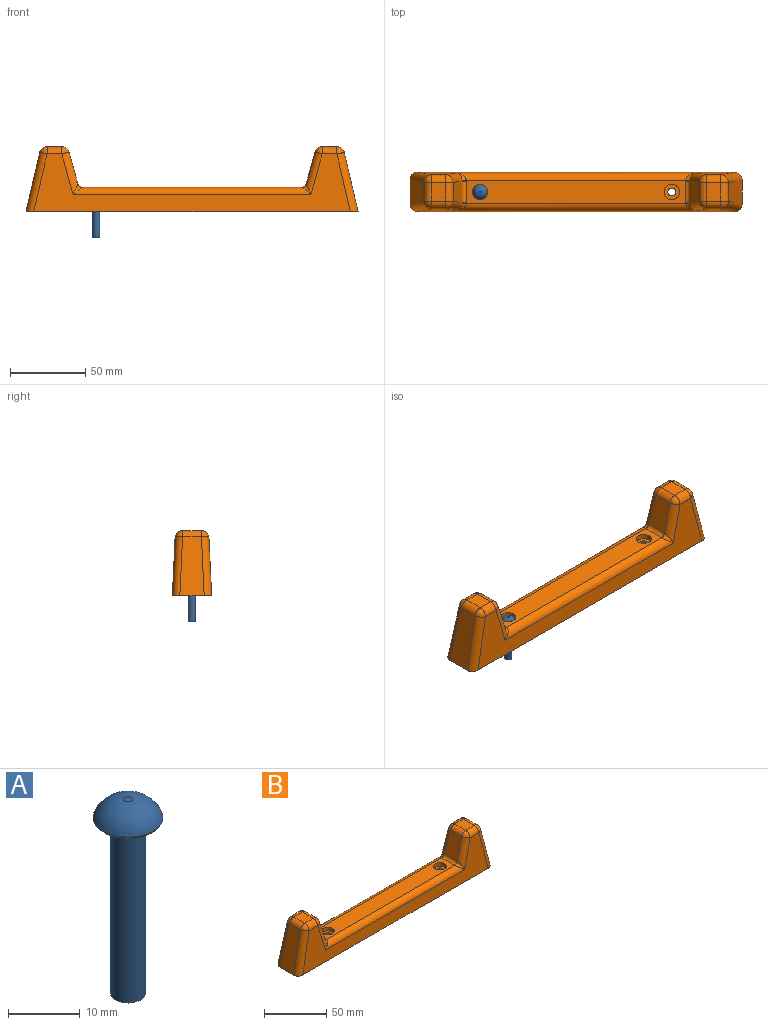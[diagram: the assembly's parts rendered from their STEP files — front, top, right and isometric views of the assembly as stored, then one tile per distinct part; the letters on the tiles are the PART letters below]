
ASSEMBLY  parts=2 mates=1
PART A: 6 faces, bbox 10.5x10.5x33 mm
  f0: cylinder r=2.45mm len=29.5mm, axis (0,0,-1), area 454.1mm2, adj f1,f2
  f1: plane 4.9x4.9mm, normal (0,0,-1), area 18.9mm2, adj f0
  f2: plane 8.7x8.7mm, normal (0,0,-1), area 40.6mm2, adj f0,f4
  f3: plane 1.21x1.21mm, normal (0,0,1), area 1.2mm2, adj f5
  f4: torus R=4.35mm, axis (0,0,1), area 23mm2, adj f2,f5
  f5: torus R=0.61mm, axis (0,0,-1), area 106mm2, adj f3,f4
PART B: 52 faces, bbox 220x26.1x43.9 mm
  f0: cylinder r=2.6mm len=12.5mm, axis (0,0,1), area 204.2mm2, adj f4,f14
  f1: cylinder r=2.6mm len=12.5mm, axis (0,0,1), area 204.2mm2, adj f4,f12
  f2: plane 12.45x9.73mm, normal (0,0,1), area 121.2mm2, adj f25,f26,f29,f30
  f3: plane 12.45x9.73mm, normal (0,0,1), area 121.2mm2, adj f33,f34,f37,f38
  f4: plane 220x26mm, normal (0,0,-1), area 5656mm2, adj f0,f1,f5,f6,f7,f8,f20,f21
  f5: plane 39.13x16.09mm, normal (-0.97,0,0.23), area 573.5mm2, adj f4,f22,f23,f30
  f6: plane 209.84x38.23mm, normal (0,-1,0.05), area 3228.5mm2, adj f4,f16,f17,f21,f22,f26,f33,f40
  f7: plane 39.13x16.09mm, normal (0.97,0,0.23), area 573.5mm2, adj f4,f20,f21,f37
  f8: plane 209.84x38.23mm, normal (0,1,0.05), area 3228.5mm2, adj f4,f18,f19,f20,f23,f29,f38,f41
  f9: plane 145.45x14.97mm, normal (0,0,1), area 2013.2mm2, adj f13,f15,f40,f41,f43,f44,f45,f48
  f10: plane 21.14x14.42mm, normal (-0.96,0,0.27), area 294.8mm2, adj f16,f18,f34,f44
  f11: plane 21.14x14.42mm, normal (0.96,0,0.27), area 294.8mm2, adj f17,f19,f25,f49
  f12: plane 10.2x10.2mm, normal (0,0,1), area 60.5mm2, adj f1,f13
  f13: cylinder r=5.1mm len=10.2mm, axis (0,0,1), area 112.2mm2, adj f9,f12
  f14: plane 10.2x10.2mm, normal (0,0,1), area 60.5mm2, adj f0,f15
  f15: cylinder r=5.1mm len=10.2mm, axis (0,0,1), area 112.2mm2, adj f9,f14
  f16: cylinder r=5mm len=28.12mm, axis (-0.27,-0.04,-0.96), area 188.5mm2, adj f6,f10,f32,f42,f43
  f17: cylinder r=5mm len=28.12mm, axis (0.27,-0.04,-0.96), area 188.5mm2, adj f6,f11,f24,f47,f48
  f18: cylinder r=5mm len=28.12mm, axis (-0.27,0.04,-0.96), area 188.5mm2, adj f8,f10,f36,f45,f46
  f19: cylinder r=5mm len=28.12mm, axis (0.27,0.04,-0.96), area 188.5mm2, adj f8,f11,f27,f50,f51
  f20: cylinder r=5mm len=40.08mm, axis (-0.23,-0.05,0.97), area 311.6mm2, adj f4,f7,f8,f39
  f21: cylinder r=5mm len=40.08mm, axis (0.23,-0.05,-0.97), area 311.6mm2, adj f4,f6,f7,f35
  f22: cylinder r=5mm len=40.08mm, axis (0.23,0.05,0.97), area 311.6mm2, adj f4,f5,f6,f28
  f23: cylinder r=5mm len=40.08mm, axis (-0.23,0.05,-0.97), area 311.6mm2, adj f4,f5,f8,f31
  f24: sphere r=5mm, area 31.4mm2, adj f17,f25,f26
  f25: cylinder r=5mm len=12.45mm, axis (0,1,0), area 80.9mm2, adj f2,f11,f24,f27
  f26: cylinder r=5mm len=9.73mm, axis (1,0,0), area 74.1mm2, adj f2,f6,f24,f28
  f27: sphere r=5mm, area 31.4mm2, adj f19,f25,f29
  f28: sphere r=5mm, area 32.4mm2, adj f22,f26,f30
  f29: cylinder r=5mm len=9.73mm, axis (1,0,0), area 74.1mm2, adj f2,f8,f27,f31
  f30: cylinder r=5mm len=12.45mm, axis (0,-1,0), area 83.6mm2, adj f2,f5,f28,f31
  f31: sphere r=5mm, area 32.4mm2, adj f23,f29,f30
  f32: sphere r=5mm, area 31.4mm2, adj f16,f33,f34
  f33: cylinder r=5mm len=9.73mm, axis (1,0,0), area 74.1mm2, adj f3,f6,f32,f35
  f34: cylinder r=5mm len=12.45mm, axis (0,1,0), area 80.9mm2, adj f3,f10,f32,f36
  f35: sphere r=5mm, area 32.4mm2, adj f21,f33,f37
  f36: sphere r=5mm, area 31.4mm2, adj f18,f34,f38
  f37: cylinder r=5mm len=12.45mm, axis (0,-1,0), area 83.6mm2, adj f3,f7,f35,f39
  f38: cylinder r=5mm len=9.73mm, axis (1,0,0), area 74.1mm2, adj f3,f8,f36,f39
  f39: sphere r=5mm, area 32.4mm2, adj f20,f37,f38
  f40: cylinder r=5mm len=157.6mm, axis (-1,0,0), area 1143.2mm2, adj f6,f9,f42,f47
  f41: cylinder r=5mm len=157.6mm, axis (-1,0,0), area 1143.2mm2, adj f8,f9,f46,f51
  f42: bspline ~6.96x6.08mm, area 20.6mm2, adj f16,f40,f43
  f43: bspline ~2.89x2.2mm, area 0.8mm2, adj f9,f16,f42,f44
  f44: cylinder r=3mm len=14.42mm, axis (0,-1,0), area 56.2mm2, adj f9,f10,f43,f45
  f45: bspline ~2.89x2.2mm, area 0.8mm2, adj f9,f18,f44,f46
  f46: bspline ~6.96x6.08mm, area 20.6mm2, adj f18,f41,f45
  f47: bspline ~6.96x6.08mm, area 20.6mm2, adj f17,f40,f48
  f48: bspline ~2.89x2.2mm, area 0.8mm2, adj f9,f17,f47,f49
  f49: cylinder r=3mm len=14.42mm, axis (0,-1,0), area 56.2mm2, adj f9,f11,f48,f50
  f50: bspline ~2.89x2.2mm, area 0.8mm2, adj f9,f19,f49,f51
  f51: bspline ~6.96x6.08mm, area 20.6mm2, adj f19,f41,f50
PLACE A t=(-86.16,-1.45,-21.05)mm
PLACE B t=(-22.66,-1.45,-4.05)mm
MATE fastened A.f0 <-> B.f1  axis (0,0,-1) through (-86.16,-1.45,-21.05)mm
